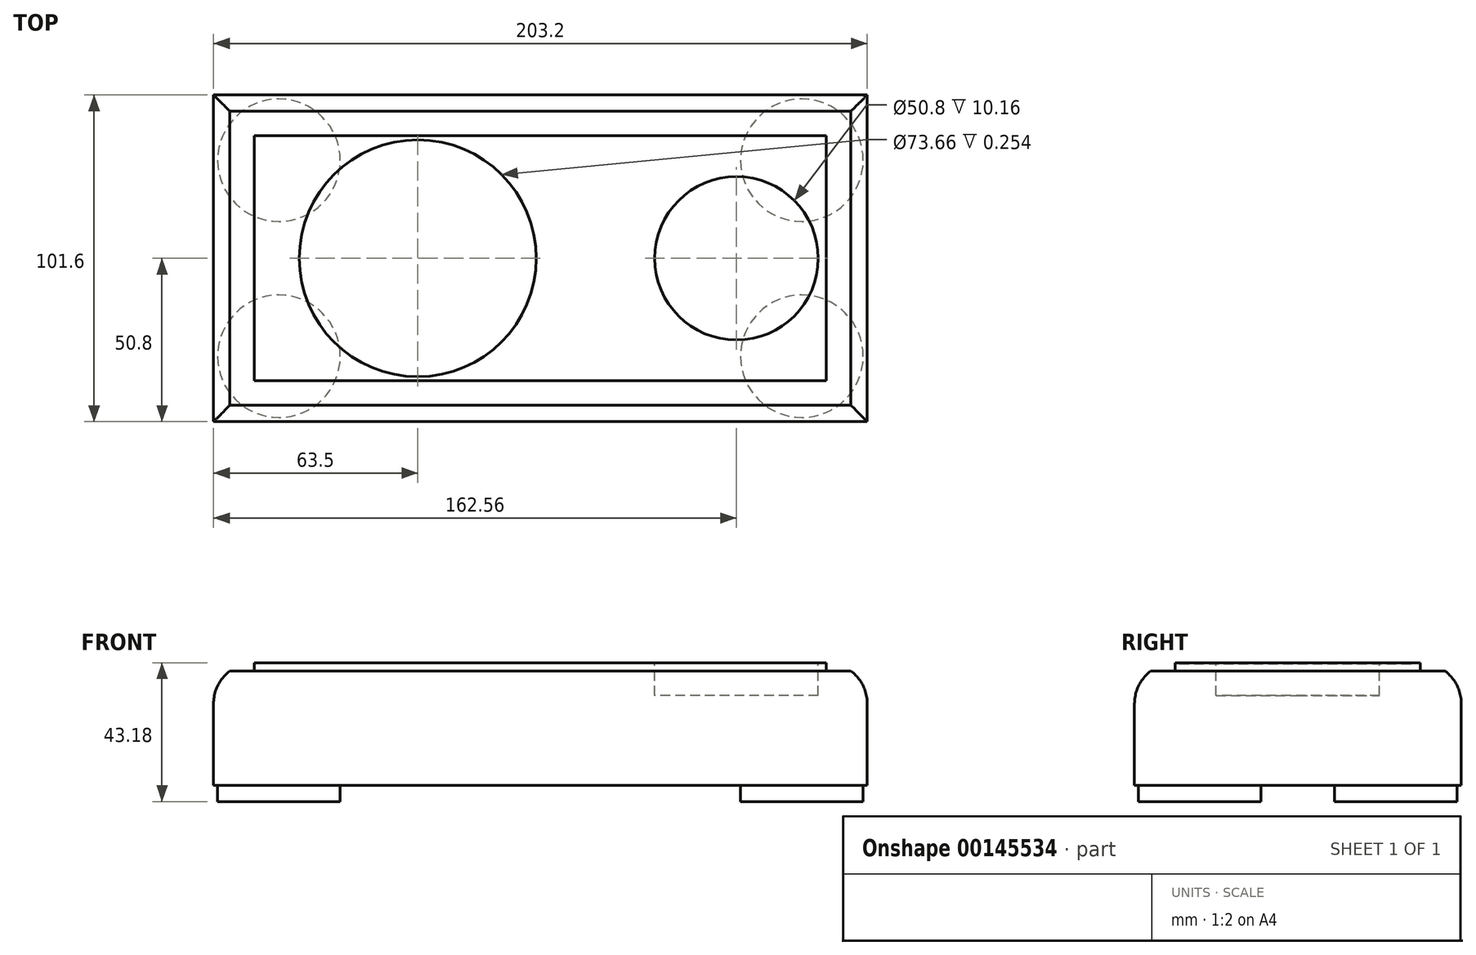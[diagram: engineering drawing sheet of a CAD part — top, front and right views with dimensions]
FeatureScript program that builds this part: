
annotation { "Feature Type Name" : "Feature", "Feature Type Description" : "" }
export const myFeature = defineFeature(function(context is Context, id is Id, definition is map)
    precondition{}
    {
        {
            var Q0;
            Q0=qCreatedBy(makeId("Top.planeOp"),FACE);
            var sketch = newSketch(context, id + "F0", { "sketchPlane" : qUnion([Q0])});
            skLineSegment(sketch, "E0.bottom", {"start": v(0, 0) * mm, "end": v(203.2, 0) * mm});
            skLineSegment(sketch, "E0.top", {"start": v(0, -101.6) * mm, "end": v(203.2, -101.6) * mm});
            skLineSegment(sketch, "E0.left", {"start": v(0, 0) * mm, "end": v(0, -101.6) * mm});
            skLineSegment(sketch, "E0.right", {"start": v(203.2, 0) * mm, "end": v(203.2, -101.6) * mm});
            skSolve(sketch);
        }
        {
            var Q0;
            Q0 = qSketchRegion(id + "F0", true);
            extrude(context, id + "F1", {"entities" : qUnion([Q0]), "depth" : 38.1 * mm});
        }
        {
            var Q0;
            Q0=makeQuery(id+"F1.opExtrude","CAP_FACE",FACE,{"disambiguationData":[OSD([sQuery(id+"F0.wireOp",EDGE,"E0.bottom"),sQuery(id+"F0.wireOp",EDGE,"E0.top"),sQuery(id+"F0.wireOp",EDGE,"E0.left"),sQuery(id+"F0.wireOp",EDGE,"E0.right")])],"isStart":true});
            var sketch = newSketch(context, id + "F2", { "sketchPlane" : qUnion([Q0])});
            skCircle(sketch, "E1", {"center": v(20.32, 81.28) * mm, "radius": 19.05 * mm});
            skCircle(sketch, "E2", {"center": v(20.32, 20.32) * mm, "radius": 19.05 * mm});
            skCircle(sketch, "E3", {"center": v(182.88, 81.28) * mm, "radius": 19.05 * mm});
            skCircle(sketch, "E4", {"center": v(182.88, 20.32) * mm, "radius": 19.05 * mm});
            skSolve(sketch);
        }
        {
            var Q0;
            Q0 = qSketchRegion(id + "F2", true);
            extrude(context, id + "F3", {"entities" : qUnion([Q0]), "depth" : 5.08 * mm});
        }
        {
            var Q0;
            Q0=makeQuery(id+"F1.opExtrude","CAP_FACE",FACE,{"disambiguationData":[OSD([sQuery(id+"F0.wireOp",EDGE,"E0.bottom"),sQuery(id+"F0.wireOp",EDGE,"E0.top"),sQuery(id+"F0.wireOp",EDGE,"E0.left"),sQuery(id+"F0.wireOp",EDGE,"E0.right")])],"isStart":false});
            fillet(context, id + "F4", {"entities" : qUnion([Q0]), "radius" : 12.7 * mm, "tangentPropagation" : true, "allowEdgeOverflow" : false});
        }
        {
            var Q0;
            Q0=makeQuery(id+"F1.opExtrude","SWEPT_FACE",FACE,{"disambiguationData":[OSD([sQuery(id+"F0.wireOp",EDGE,"E0.right")])]});
            var sketch = newSketch(context, id + "F5", { "sketchPlane" : qUnion([Q0])});
            skLineSegment(sketch, "E5.0", {"start": v(-88.9, 38.1) * mm, "end": v(-12.7, 38.1) * mm});
            skLineSegment(sketch, "E6.bottom", {"start": v(-12.7, 38.1) * mm, "end": v(0, 38.1) * mm});
            skLineSegment(sketch, "E6.top", {"start": v(-12.7, 35.56) * mm, "end": v(0, 35.56) * mm});
            skLineSegment(sketch, "E6.left", {"start": v(-12.7, 38.1) * mm, "end": v(-12.7, 35.56) * mm});
            skLineSegment(sketch, "E6.right", {"start": v(0, 38.1) * mm, "end": v(0, 35.56) * mm});
            skLineSegment(sketch, "E7.bottom", {"start": v(-88.9, 38.1) * mm, "end": v(-101.6, 38.1) * mm});
            skLineSegment(sketch, "E7.top", {"start": v(-88.9, 35.56) * mm, "end": v(-101.6, 35.56) * mm});
            skLineSegment(sketch, "E7.left", {"start": v(-88.9, 38.1) * mm, "end": v(-88.9, 35.56) * mm});
            skLineSegment(sketch, "E7.right", {"start": v(-101.6, 38.1) * mm, "end": v(-101.6, 35.56) * mm});
            skSolve(sketch);
        }
        {
            var Q0;
            Q0 = qSketchRegion(id + "F5", true);
            extrude(context, id + "F6", {"entities" : qUnion([Q0]), "operationType" : NewBodyOperationType.REMOVE, "endBound" : BoundingType.THROUGH_ALL, "oppositeDirection" : true, "depth" : 25.4 * mm});
        }
        {
            var Q0;
            Q0=makeQuery(id+"F1.opExtrude","SWEPT_FACE",FACE,{"disambiguationData":[OSD([sQuery(id+"F0.wireOp",EDGE,"E0.top")])]});
            var sketch = newSketch(context, id + "F7", { "sketchPlane" : qUnion([Q0])});
            skLineSegment(sketch, "E8.0", {"start": v(12.7, 38.1) * mm, "end": v(190.5, 38.1) * mm});
            skLineSegment(sketch, "E9.bottom", {"start": v(0, 38.1) * mm, "end": v(12.7, 38.1) * mm});
            skLineSegment(sketch, "E9.top", {"start": v(0, 35.56) * mm, "end": v(12.7, 35.56) * mm});
            skLineSegment(sketch, "E9.left", {"start": v(0, 38.1) * mm, "end": v(0, 35.56) * mm});
            skLineSegment(sketch, "E9.right", {"start": v(12.7, 38.1) * mm, "end": v(12.7, 35.56) * mm});
            skLineSegment(sketch, "E10.bottom", {"start": v(190.5, 38.1) * mm, "end": v(203.2, 38.1) * mm});
            skLineSegment(sketch, "E10.top", {"start": v(190.5, 35.56) * mm, "end": v(203.2, 35.56) * mm});
            skLineSegment(sketch, "E10.left", {"start": v(190.5, 38.1) * mm, "end": v(190.5, 35.56) * mm});
            skLineSegment(sketch, "E10.right", {"start": v(203.2, 38.1) * mm, "end": v(203.2, 35.56) * mm});
            skSolve(sketch);
        }
        {
            var Q0;
            Q0 = qSketchRegion(id + "F7", true);
            extrude(context, id + "F8", {"entities" : qUnion([Q0]), "operationType" : NewBodyOperationType.REMOVE, "endBound" : BoundingType.THROUGH_ALL, "oppositeDirection" : true, "depth" : 25.4 * mm});
        }
        {
            var Q0;
            Q0=makeQuery(id+"F1.opExtrude","CAP_FACE",FACE,{"disambiguationData":[OSD([sQuery(id+"F0.wireOp",EDGE,"E0.bottom"),sQuery(id+"F0.wireOp",EDGE,"E0.top"),sQuery(id+"F0.wireOp",EDGE,"E0.left"),sQuery(id+"F0.wireOp",EDGE,"E0.right")])],"isStart":false});
            var sketch = newSketch(context, id + "F9", { "sketchPlane" : qUnion([Q0])});
            skLineSegment(sketch, "E11.bottom", {"start": v(12.7, -12.7) * mm, "end": v(190.5, -12.7) * mm});
            skLineSegment(sketch, "E11.top", {"start": v(12.7, -88.9) * mm, "end": v(190.5, -88.9) * mm});
            skLineSegment(sketch, "E11.left", {"start": v(12.7, -12.7) * mm, "end": v(12.7, -88.9) * mm});
            skLineSegment(sketch, "E11.right", {"start": v(190.5, -12.7) * mm, "end": v(190.5, -88.9) * mm});
            skCircle(sketch, "E12", {"center": v(162.56, -50.8) * mm, "radius": 25.4 * mm});
            skSolve(sketch);
        }
        {
            var Q0;
            Q0=makeQuery(id+"F9.imprint","IMPRINT",FACE,{"disambiguationData":[TD([[makeQuery(id+"F9.imprint","IMPRINT",EDGE,{"derivedFrom":sQuery(id+"F9.wireOp",EDGE,"E12")}),1.0]])]});
            extrude(context, id + "F10", {"entities" : qUnion([Q0]), "operationType" : NewBodyOperationType.REMOVE, "oppositeDirection" : true, "depth" : 10.16 * mm});
        }
        {
            var Q0;
            Q0=makeQuery(id+"F1.opExtrude","CAP_FACE",FACE,{"disambiguationData":[OSD([sQuery(id+"F0.wireOp",EDGE,"E0.bottom"),sQuery(id+"F0.wireOp",EDGE,"E0.top"),sQuery(id+"F0.wireOp",EDGE,"E0.left"),sQuery(id+"F0.wireOp",EDGE,"E0.right")])],"isStart":false});
            var sketch = newSketch(context, id + "F11", { "sketchPlane" : qUnion([Q0])});
            skCircle(sketch, "E13", {"center": v(63.5, -50.8) * mm, "radius": 36.83 * mm});
            skSolve(sketch);
        }
        {
            var Q0;
            Q0 = qSketchRegion(id + "F11", true);
            extrude(context, id + "F12", {"entities" : qUnion([Q0]), "operationType" : NewBodyOperationType.REMOVE, "oppositeDirection" : true, "depth" : 0.25 * mm});
        }
    });
